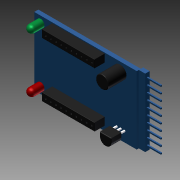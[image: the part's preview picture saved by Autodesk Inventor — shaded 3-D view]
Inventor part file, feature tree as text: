
AUTODESK INVENTOR PART (.ipt)
format: ipt  version: 2012 (Build 160160000, 160)  size: 500,224 bytes
history: native  units: in
note: dims shown in document units (in); Inventor stores cm internally (conversion verified against a paired STEP export)
features: extrude x9, fillet x4, sketch x3
ambient origin geometry x8: Origin, YZ Plane, XZ Plane, XY Plane, X Axis, Y Axis, Z Axis, Center Point
bodies: Solid1 (feature_tree)
feature tree (16):
  sketch  "Sketch1"  dims[d0=1.5748in d1=1.0433in]
  extrude  "Extrusion1"  Depth=1.0433in
  extrude  "Extrusion2"  Depth=0.1181in
  extrude  "Extrusion3"  Depth=0.1181in
  fillet  "Fillet1"  Radius=0.1181in
  fillet  "Fillet2"  Radius=0.0394in
  extrude  "Extrusion5"  Depth=0.0394in
  sketch  "Sketch3"  dims[d3=0.8071in d4=0.1181in]
  extrude  "Extrusion8"  Depth=0.1969in
  extrude  "Extrusion9"  Depth=0.1575in
  extrude  "Extrusion10"  Depth=0.0394in
  extrude  "Extrusion11"  Depth=0.063in TaperAngle=0.0deg
  fillet  "Fillet6"  Radius=0.2756in
  extrude  "Extrusion12"  Depth=0.1969in TaperAngle=0.0deg
  fillet  "Fillet7"  Radius=0.059in
  sketch  "Sketch4"  dims[d6=0.2756in d8=0.1181in d9=0.1181in d10=0.0394in d11=0.0394in d12=0.1969in d13=0.1575in d14=0.0394in d15=0.063in d16=0.0in d17=0.2756in d18=0.0in d19=0.1969in d20=0.0in d21=0.059in d22=0.01in d23=0.0591in d24=0.1772in d28=0.0394in d29=0.1575in d33=0.0197in d34=0.0197in d35=0.0197in d36=0.0197in d37=0.0197in d38=0.0197in d39=0.0394in d40=0.0394in d41=0.0197in d42=0.0197in d43=0.0197in d44=0.018in d45=0.0787in d46=0.0in d56=0.042in d58=0.042in d122=1.0433in d123=0.0669in d124=0.0197in d125=0.0197in d126=0.0615in d127=0.0236in d128=0.0197in d129=0.0197in d130=0.0197in d131=0.0197in d145=0.0236in d147=0.0236in d148=0.0197in d149=0.0197in d150=0.1in d151=0.0236in d152=0.1in d154=0.0197in d155=0.0197in d156=0.1in d157=0.0236in d158=0.0197in d159=0.0197in d160=0.1in d161=0.0236in d162=0.1in d163=0.0197in d164=0.0197in d166=0.1in d167=0.0236in d168=0.0197in d169=0.0197in d170=0.1in d171=0.0236in d172=0.0197in d173=0.0197in d174=0.1in d175=0.0236in d176=0.0197in d177=0.0197in d178=0.1in d179=0.0236in d180=0.315in d181=0.0in d182=0.0984in d183=0.0in d184=0.1181in d185=0.0in d191=0.0236in d192=0.0236in d193=0.043in d194=0.0472in d195=0.0236in d196=0.0236in d197=0.0787in d198=0.0472in d199=0.0236in d200=0.0236in d202=0.0472in d203=0.0236in d204=0.0236in d205=0.0787in d206=0.0787in d207=0.0787in d208=0.0236in d209=0.0236in d210=0.0472in d211=0.0236in d212=0.0236in d213=0.0787in d214=0.0472in d215=0.0236in d216=0.0236in d217=0.0787in d218=0.0472in d219=0.0236in d220=0.0236in d221=0.0787in d222=0.0472in d223=0.0236in d224=0.0236in d225=0.0787in d226=0.0472in d227=0.0236in d228=0.0236in d229=0.0787in d230=0.0472in d231=0.8071in d232=0.1181in d233=0.0236in d234=0.0236in d235=0.043in d236=0.0472in d237=0.0236in d238=0.0236in d239=0.0787in d240=0.0472in d241=0.0236in d242=0.0236in d243=0.0472in d244=0.0236in d245=0.0236in d246=0.0787in d247=0.0787in d248=0.0787in d249=0.0236in d250=0.0236in d251=0.0472in d252=0.0236in d253=0.0236in d254=0.0787in d255=0.0472in d256=0.0236in d257=0.0236in d258=0.0787in d259=0.0472in d260=0.0236in d261=0.0236in d262=0.0787in d263=0.0472in d264=0.0236in d265=0.0236in d266=0.0787in d267=0.0472in d268=0.0236in d269=0.0236in d270=0.0787in d271=0.0472in d274=0.7224in d275=0.2756in d276=0.1575in d277=0.0in d278=0.005in d279=0.1575in d280=0.0in d281=0.01in]
